# Revit family: Haworth_BackWing_LoungeChair_PRELIMINARY
name_source: partatom
category: Furniture
revit_build: Autodesk Revit 2018 (Build: 20170223_1515(x64)
units: mm (PartAtom-declared; Revit-internal decimal feet)

## family parameters
Always vertical = Yes
Cut with Voids When Loaded = No
OmniClass Number = 23.40.70.14.64.21
OmniClass Title = Systems Furniture
Room Calculation Point = No
Shared = No
Work Plane-Based = No

## types (1)
- Back-Wing
    Actual Depth = 28 205/256"
    Actual Height = 27 51/128"
    Actual Width = 35 179/256"
    Assembly Code = E2020200
    Description = Haworth - Cassina - Back-Wing - Lounge Chair
    Manufacturer = Haworth
    Model = HCCSBWL1
    Revision Number = 1
    Seat Height = 17"
    Size = Verify Final Dim. w/ Haworth
    Sustainability Info = https://www.haworth.com
    URL = https://www.haworth.com
    URL - Product = https://www.haworth.com
    Warranty = http://www.haworth.com

## geometry (parser evidence)
native form markers: Sweep x1
no freeform markers — native parametric forms only
